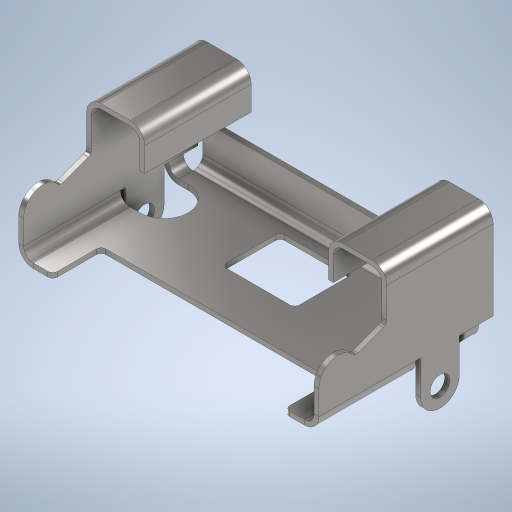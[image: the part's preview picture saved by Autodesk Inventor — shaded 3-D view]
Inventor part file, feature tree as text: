
AUTODESK INVENTOR PART (.ipt)
format: ipt  version: 2024 (Build 280153000, 153)  size: 512,000 bytes
history: native  units: mm
features: sheet_metal_op x25, other x14, sketch x12
ambient origin geometry x8: Origin, YZ Plane, XZ Plane, XY Plane, X Axis, Y Axis, Z Axis, Center Point
bodies: Solid1 (feature_tree)
feature tree (51):
  sheet_metal_op  "Face1"
  sheet_metal_op  "Flange1"
  sheet_metal_op  "Flange2"
  sheet_metal_op  "Flange3"
  sheet_metal_op  "Flange4"
  sheet_metal_op  "Flange5"
  sheet_metal_op  "Flange6"
  sheet_metal_op  "Flange7"
  other  "Full Round Fillet1"
  other  "Full Round Fillet2"
  sheet_metal_op  "Flange8"
  sketch  "Sketch1"  dims[d0=72.0mm]
  other  "Plate1"
  sketch  "Sketch2"  dims[d1=124.0mm]
  other  "Plate2"
  sheet_metal_op  "Bend1"
  sheet_metal_op  "Corner1"
  sketch  "Sketch3"  dims[d2=14.0mm]
  other  "Plate3"
  sheet_metal_op  "Bend2"
  sheet_metal_op  "Corner2"
  sketch  "Sketch4"  dims[d3=20.0mm]
  other  "Plate4"
  sheet_metal_op  "Bend3"
  sheet_metal_op  "Corner3"
  sketch  "Sketch5"  dims[d4=96.0mm]
  other  "Plate5"
  sheet_metal_op  "Bend4"
  sheet_metal_op  "Corner4"
  sketch  "Sketch6"  dims[d5=24.0mm]
  other  "Plate6"
  sheet_metal_op  "Bend5"
  sheet_metal_op  "Corner5"
  sketch  "Sketch7"  dims[d6=30.0mm]
  other  "Plate7"
  sheet_metal_op  "Bend6"
  sheet_metal_op  "Corner6"
  sketch  "Sketch10"  dims[d7=2.0mm]
  sketch  "Sketch11"  dims[d8=2.0mm]
  other  "Plate8"
  sheet_metal_op  "Bend7"
  sheet_metal_op  "Corner7"
  sketch  "Sketch12"  dims[d9=22.0mm]
  sketch  "Sketch13"  dims[d10=2.0mm]
  sketch  "Sketch14"  dims[d11=2.0mm d12=1.0mm d13=4.0mm d14=2.0mm d15=45.0mm d16=90.0deg d17=4.0mm d18=8.0mm d19=2.0mm d20=2.0mm d21=2.0mm d22=1.0mm d23=4.0mm d24=2.0mm d25=45.0mm d26=90.0deg d27=4.0mm d28=8.0mm d29=2.0mm d30=2.0mm d31=2.0mm d32=1.0mm d33=4.0mm d34=2.0mm d35=24.0mm d36=90.0deg d37=4.0mm d38=8.0mm d39=2.0mm d40=2.0mm d41=2.0mm d42=1.0mm d43=4.0mm d44=2.0mm d45=24.0mm d46=90.0deg d47=4.0mm d48=8.0mm d49=2.0mm d50=2.0mm d51=2.0mm d52=1.0mm d53=4.0mm d54=2.0mm d55=16.0mm d56=90.0deg d57=4.0mm d58=8.0mm d59=2.0mm d60=2.0mm d61=2.0mm d62=1.0mm d63=4.0mm d64=2.0mm d65=16.0mm d66=90.0deg d67=4.0mm d68=8.0mm d69=2.0mm d70=2.0mm d71=10.0mm d72=20.0mm d73=22.0mm d74=20.0mm d75=10.0mm d76=10.0mm d77=22.0mm d78=6.0mm d79=0.0mm d80=2.0mm d81=1.0mm d82=4.0mm d83=2.0mm d84=22.0mm d85=0.0mm d86=0.0mm d87=8.0mm d88=2.0mm d89=2.0mm d90=44.0mm d91=20.0mm d93=27.925268mm d94=16.0mm d95=16.0mm d96=2.0mm d97=2.0mm d98=124.0mm d99=0.0mm d100=8.0mm d101=8.0mm d102=8.0mm d103=124.0mm d104=0.0mm d105=2.0mm d106=1.0mm d107=4.0mm d108=2.0mm d109=18.0mm d110=90.0deg d111=4.0mm d112=8.0mm d113=2.0mm d114=2.0mm]
  other  "Plate9"
  sheet_metal_op  "Bend8"
  sheet_metal_op  "Corner8"
  other  "Cut1"
  other  "Cut2"
  other  "Cut3"
